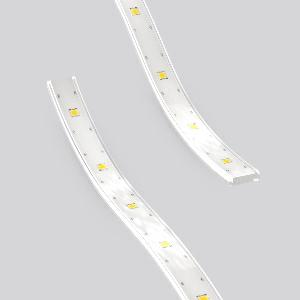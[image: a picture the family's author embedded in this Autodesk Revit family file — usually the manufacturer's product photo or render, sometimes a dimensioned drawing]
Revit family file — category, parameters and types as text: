
# Revit family: led_it_strip_982520_002_5652
name_source: partatom
category: Lighting Fixtures
units: mm (PartAtom-declared; Revit-internal decimal feet)

## family parameters
Cut with Voids When Loaded = No
Host = Face
Light Source = No
Part Type = Normal
Room Calculation Point = No
Round Connector Dimension = Use Diameter
Shared = No

## types (1)
- LED IT STRIP (1 x LED Modul 830, 370 lm, 3000)
    Apparent Load = 4 VA
    Approval mark = CE
    CIE Flux Codes = 51 84 98 100 100
    Color Rendering = 80
    Color Temperature = 3000
    Default Elevation = 1800 mm
    Description = Series: LED IT STRIP
Flexible fully encapsulated LED strip for indoor and outdoor use. UV/IR resistant TPU potting. LED Pitch 35.7 mm. Solderless connection technology by means of Plug+Play connector system. No need for silicone sealing. Easy separability with commercially available tools (every 250 mm). Smallest bending radius 60 mm. Up to 20 meters LED strip length with only one power supply. One power feed and one end cap included, other accessories can be ordered separately. 
Colour: white
Length: 5000 mm
Width: 12 mm
Height: 3.4 mm
Lamp: LED
Socket: without socket
Colour temperature: 3000K
Colour rendering index (CRI): 80
System power: 4 W
Rated luminous flux: 370 lm
Luminous efficiency: 93 lm/W
Protection class: III
Type of protection: IP 65
    Height = 3 mm  [stored 0.00984252 ft]
    Lamp = 1 x LED Modul 830
    Lamp Light Flux = 370 lm
    Lamp count = 1
    Length = 5000 mm
    Lifetime = 50000 h
    Luminous efficacy = 93 lm/W
    Manufacturer = RZB
    ModVariant = No
    Model = 982520.002
    Mounting Place = Ceiling, Wall
    Mounting Type = Surface mounted
    Number of Poles = 1
    OnlyDefault = Yes
    Power Factor = 1
    Product Name = LED IT STRIP
    Product group = Surface mounted LED linear luminaires
    ProductGroupID = 307
    Protection Class = Safety extra-low voltage
    Protection Degree = IP 65
    RLX_Detail_Level = 1
    RLX_Emergency_Light_Flux = 0 lm
    RLX_Emergency_Type = 0
    RLX_Emergency_Type_DB = No
    RlxData = <blob elided: 30785 chars, md5=7117baf2>
    Socket = socket
    Standby Power = 0 W
    System Light Flux = 370 lm
    System Power = 4 W
    Type Comments = Product without accessories
    Type Image = 982520.002.jpg
    URL = http://relux.com
    VarID = ---
    Voltage = 24 V
    Voltage Range = 24 V
    Weight = 0.00 kg
    Width = 12 mm  [stored 0.0393701 ft]

note: [stored X ft] marks values corroborated as IEEE doubles in the binary element streams (Revit-internal decimal feet)

## geometry (parser evidence)
native form markers: Blend x4, Sweep x11
no freeform markers — native parametric forms only
